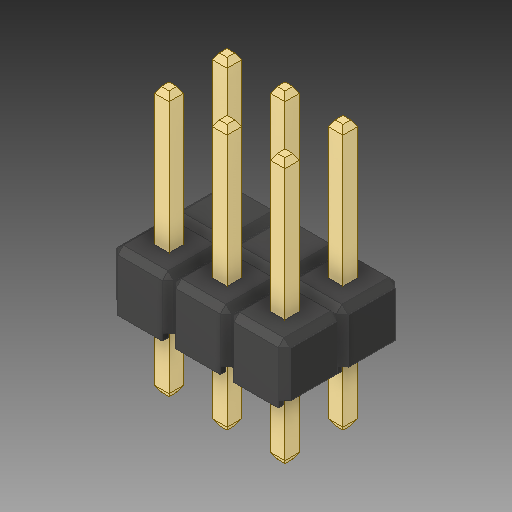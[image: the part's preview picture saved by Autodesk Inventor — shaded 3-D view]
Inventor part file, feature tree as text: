
AUTODESK INVENTOR PART (.ipt)
format: ipt  version: 2019 (Build 230136000, 136)  size: 273,408 bytes
history: native  units: in
note: dims shown in document units (in); Inventor stores cm internally (conversion verified against a paired STEP export)
features: other x11, chamfer x1
ambient origin geometry x8: Origin, YZ Plane, XZ Plane, XY Plane, X Axis, Y Axis, Z Axis, Center Point
bodies: Solid1 (feature_tree), Solid2 (feature_tree), Solid3 (feature_tree), Solid4 (feature_tree), Solid5 (feature_tree), Solid6 (feature_tree), Solid7 (feature_tree), Solid8 (feature_tree), Solid9 (feature_tree), Solid10 (feature_tree), Solid11 (feature_tree), Solid12 (feature_tree)
feature tree (12):
  chamfer  "Chamfer2"  [1 undecoded]
  other  "Boss-Extrude3"
  other  "LPattern1[1]"
  other  "LPattern1[2]"
  other  "LPattern1[3]"
  other  "LPattern1[4]"
  other  "LPattern1[5]"
  other  "LPattern1[6]"
  other  "LPattern1[7]"
  other  "LPattern1[8]"
  other  "LPattern1[9]"
  other  "LPattern1[10]"
note: 1 required parameter value undecoded (feature->parameter linkage not recoverable at this tier; creation-order binding heuristic only, values carry confidence <= 0.55)
